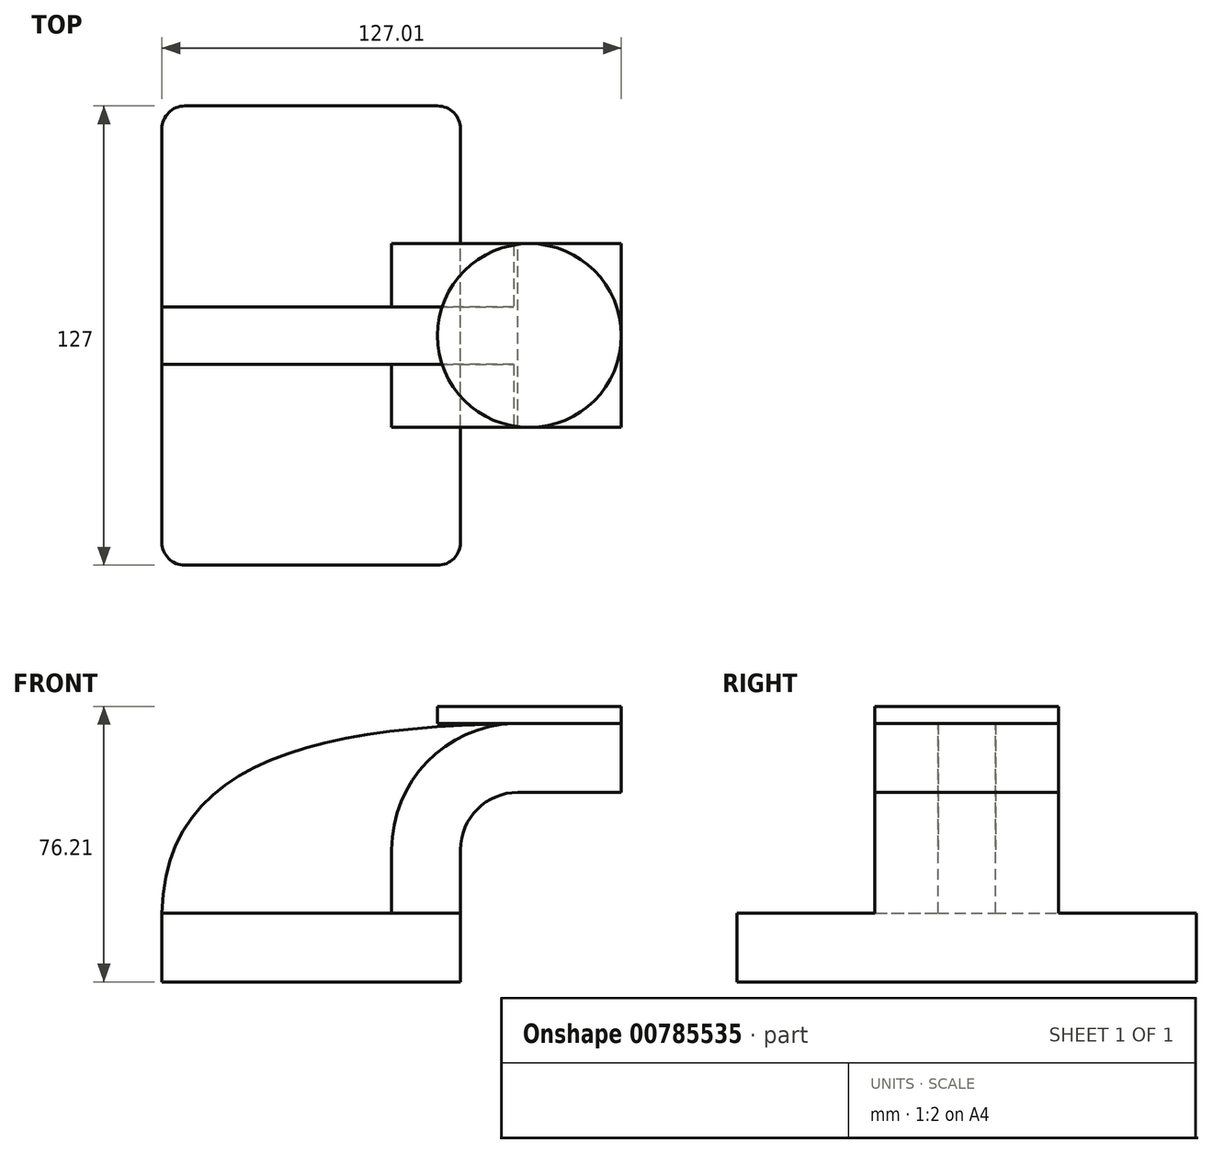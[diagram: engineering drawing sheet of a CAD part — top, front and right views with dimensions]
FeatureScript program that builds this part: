
annotation { "Feature Type Name" : "Feature", "Feature Type Description" : "" }
export const myFeature = defineFeature(function(context is Context, id is Id, definition is map)
    precondition{}
    {
        {
            var Q0;
            Q0=qCreatedBy(makeId("Front.planeOp"),FACE);
            var sketch = newSketch(context, id + "F0", { "sketchPlane" : qUnion([Q0])});
            skLineSegment(sketch, "E0.bottom", {"start": v(41.28, -9.52) * mm, "end": v(-41.28, -9.53) * mm});
            skLineSegment(sketch, "E0.top", {"start": v(41.27, 9.53) * mm, "end": v(-41.28, 9.53) * mm});
            skLineSegment(sketch, "E0.left", {"start": v(41.27, -9.52) * mm, "end": v(41.27, 9.53) * mm});
            skLineSegment(sketch, "E0.right", {"start": v(-41.28, -9.52) * mm, "end": v(-41.28, 9.53) * mm});
            skPoint(sketch, "E0.middle", {"position": v(0, 0) * mm});
            skLineSegment(sketch, "E1.bottom", {"start": v(111.12, 38.1) * mm, "end": v(60.32, 38.1) * mm});
            skLineSegment(sketch, "E1.top", {"start": v(111.12, 66.68) * mm, "end": v(60.32, 66.68) * mm});
            skLineSegment(sketch, "E1.left", {"start": v(111.12, 38.1) * mm, "end": v(111.12, 66.68) * mm});
            skLineSegment(sketch, "E1.right", {"start": v(60.32, 38.1) * mm, "end": v(60.32, 66.68) * mm});
            skPoint(sketch, "E1.middle", {"position": v(85.72, 52.39) * mm});
            skLineSegment(sketch, "E2", {"start": v(41.27, 9.52) * mm, "end": v(41.27, 27) * mm});
            skArc(sketch, "E3", {"start": v(41.27, 27) * mm, "mid": v(45.92, 38.23) * mm, "end": v(57.15, 42.88) * mm});
            skLineSegment(sketch, "E4", {"start": v(57.15, 42.88) * mm, "end": v(85.72, 42.88) * mm});
            skLineSegment(sketch, "E5.0", {"start": v(57.15, 61.93) * mm, "end": v(85.72, 61.93) * mm});
            skArc(sketch, "E5.1", {"start": v(22.23, 27) * mm, "mid": v(32.45, 51.7) * mm, "end": v(57.15, 61.93) * mm});
            skLineSegment(sketch, "E5.2", {"start": v(22.23, 9.53) * mm, "end": v(22.23, 27) * mm});
            skLineSegment(sketch, "E6", {"start": v(85.72, 42.88) * mm, "end": v(85.72, 61.93) * mm});
            skFitSpline(sketch, "E7", {"points": [v(-41.28, 9.53) * mm, v(57.15, 61.93) * mm], "startDerivative": vector(2.24, 124.35) * mm, "endDerivative": vector(171.45, 2.75) * mm});
            skLineSegment(sketch, "E8", {"start": v(85.72, 47.92) * mm, "end": v(85.72, 38.1) * mm});
            skLineSegment(sketch, "E9", {"start": v(85.72, 38.1) * mm, "end": v(85.72, 66.68) * mm});
            skSolve(sketch);
        }
        {
            var Q0;
            Q0=makeQuery(id+"F0.imprint","IMPRINT",FACE,{"disambiguationData":[TD([[makeQuery(id+"F0.imprint","IMPRINT",EDGE,{"derivedFrom":sQuery(id+"F0.wireOp",EDGE,"E0.bottom")}),-1.0]])]});
            extrude(context, id + "F1", {"entities" : qUnion([Q0]), "endBound" : BoundingType.SYMMETRIC, "depth" : 127 * mm, "offsetDistance" : 25.4 * mm});
        }
        {
            var Q0;
            {var subQ1=sQuery(id+"F0.wireOp",EDGE,"E2");Q0=makeQuery(id+"F0.imprint","IMPRINT",FACE,{"disambiguationData":[TD([[makeQuery(id+"F0.imprint","IMPRINT",EDGE,{"derivedFrom":subQ1}),1.0]])]});}
            var Q1;
            {var subQ5=sQuery(id+"F0.wireOp",EDGE,"E6");Q1=makeQuery(id+"F0.imprint","IMPRINT",FACE,{"disambiguationData":[TD([[makeQuery(id+"F0.imprint","IMPRINT",EDGE,{"derivedFrom":subQ5}),1.0]])]});}
            extrude(context, id + "F2", {"entities" : qUnion([Q0, Q1]), "operationType" : NewBodyOperationType.ADD, "endBound" : BoundingType.SYMMETRIC, "depth" : 50.8 * mm, "offsetDistance" : 25.4 * mm});
        }
        {
            var Q0;
            {var subQ3=sQuery(id+"F0.wireOp",EDGE,"E5.2");Q0=makeQuery(id+"F0.imprint","IMPRINT",FACE,{"disambiguationData":[TD([[makeQuery(id+"F0.imprint","IMPRINT",EDGE,{"derivedFrom":subQ3}),1.0]])]});}
            extrude(context, id + "F3", {"entities" : qUnion([Q0]), "operationType" : NewBodyOperationType.ADD, "endBound" : BoundingType.SYMMETRIC, "depth" : 15.88 * mm, "offsetDistance" : 25.4 * mm});
        }
        {
            var Q0;
            {var subQ0=sQuery(id+"F0.wireOp",EDGE,"E9");var subQ3=makeQuery(id+"F0.imprint","IMPRINT",VERTEX,{"derivedFrom":subQ0});Q0=makeQuery(id+"F0.imprint","IMPRINT",FACE,{"disambiguationData":[TD([[makeQuery(id+"F0.imprint","IMPRINT",EDGE,{"disambiguationData":[TD([[subQ3,1.0]])],"derivedFrom":subQ0}),1.0]])]});}
            var Q1;
            Q1=sQuery(id+"F0.wireOp",EDGE,"E1.right");
            revolve(context, id + "F4", {"operationType" : NewBodyOperationType.ADD, "surfaceOperationType" : NewSurfaceOperationType.NEW, "entities" : qUnion([Q0]), "axis" : qUnion([Q1]), "revolveType" : RevolveType.FULL});
        }
        {
            var Q0;
            Q0=makeQuery(id+"F1.opExtrude","CAP_EDGE",EDGE,{"disambiguationData":[OSD([sQuery(id+"F0.wireOp",EDGE,"E0.left")])],"isStart":false});
            var Q1;
            Q1=makeQuery(id+"F1.opExtrude","CAP_EDGE",EDGE,{"disambiguationData":[OSD([sQuery(id+"F0.wireOp",EDGE,"E0.right")])],"isStart":false});
            var Q2;
            Q2=makeQuery(id+"F1.opExtrude","CAP_EDGE",EDGE,{"disambiguationData":[OSD([sQuery(id+"F0.wireOp",EDGE,"E0.left")])],"isStart":true});
            var Q3;
            Q3=makeQuery(id+"F1.opExtrude","CAP_EDGE",EDGE,{"disambiguationData":[OSD([sQuery(id+"F0.wireOp",EDGE,"E0.right")])],"isStart":true});
            fillet(context, id + "F5", {"entities" : qUnion([Q0, Q1, Q2, Q3]), "radius" : 6.35 * mm, "tangentPropagation" : true, "allowEdgeOverflow" : false});
        }
    });
